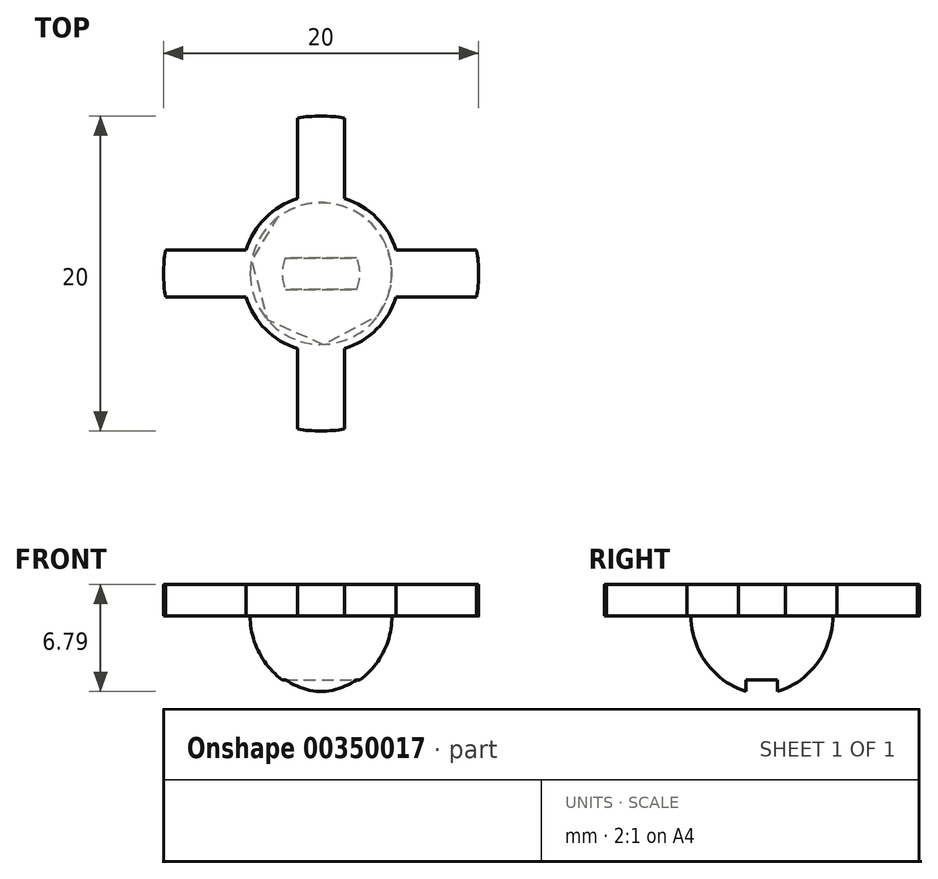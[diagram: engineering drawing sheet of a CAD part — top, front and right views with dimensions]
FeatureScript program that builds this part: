
annotation { "Feature Type Name" : "Feature", "Feature Type Description" : "" }
export const myFeature = defineFeature(function(context is Context, id is Id, definition is map)
    precondition{}
    {
        {
            var Q0;
            Q0=qCreatedBy(makeId("Top.planeOp"),FACE);
            var sketch = newSketch(context, id + "F0", { "sketchPlane" : qUnion([Q0])});
            skCircle(sketch, "E0", {"center": v(0, 0) * mm, "radius": 10 * mm});
            skSolve(sketch);
        }
        {
            var Q0;
            Q0=makeQuery(id+"F0.imprint","IMPRINT",FACE,{"disambiguationData":[TD([[makeQuery(id+"F0.imprint","IMPRINT",EDGE,{"derivedFrom":sQuery(id+"F0.wireOp",EDGE,"E0")}),1.0]])]});
            var Q1;
            Q1=sQuery(id+"F0.wireOp",EDGE,"E0");
            extrude(context, id + "F1", {"entities" : qUnion([Q0]), "surfaceEntities" : qUnion([Q1]), "depth" : 2 * mm});
        }
        {
            var Q0;
            Q0=makeQuery(id+"F1.opExtrude","CAP_FACE",FACE,{"disambiguationData":[OSD([sQuery(id+"F0.wireOp",EDGE,"E0")])],"isStart":false});
            var sketch = newSketch(context, id + "F2", { "sketchPlane" : qUnion([Q0])});
            skCircle(sketch, "E1", {"center": v(0, 0) * mm, "radius": 5 * mm});
            skLineSegment(sketch, "E2.bottom", {"start": v(-1.5, 10) * mm, "end": v(1.5, 10) * mm});
            skLineSegment(sketch, "E2.top", {"start": v(-1.5, -10) * mm, "end": v(1.5, -10) * mm});
            skLineSegment(sketch, "E2.left", {"start": v(-1.5, 10) * mm, "end": v(-1.5, -10) * mm});
            skLineSegment(sketch, "E2.right", {"start": v(1.5, 10) * mm, "end": v(1.5, -10) * mm});
            skLineSegment(sketch, "E3", {"start": v(0, 10) * mm, "end": v(0, -10) * mm, "construction": true});
            skLineSegment(sketch, "E4", {"start": v(-10, 0) * mm, "end": v(10, 0) * mm, "construction": true});
            skLineSegment(sketch, "E5.bottom", {"start": v(-10, 1.5) * mm, "end": v(10, 1.5) * mm});
            skLineSegment(sketch, "E5.top", {"start": v(-10, -1.5) * mm, "end": v(10, -1.5) * mm});
            skLineSegment(sketch, "E5.left", {"start": v(-10, 1.5) * mm, "end": v(-10, -1.5) * mm});
            skLineSegment(sketch, "E5.right", {"start": v(10, 1.5) * mm, "end": v(10, -1.5) * mm});
            skSolve(sketch);
        }
        {
            var Q0;
            {var subQ0=sQuery(id+"F2.wireOp",EDGE,"E2.left");var subQ1=sQuery(id+"F2.wireOp",EDGE,"E1");var subQ2=makeQuery(id+"F2.imprint","INTERSECT",VERTEX,{"disambiguationData":[OD(0.0)],"derivedFrom":[subQ1,subQ0]});Q0=makeQuery(id+"F2.imprint","IMPRINT",FACE,{"disambiguationData":[TD([[makeQuery(id+"F2.imprint","IMPRINT",EDGE,{"disambiguationData":[TD([[subQ2,-1.0]])],"derivedFrom":subQ1}),-1.0]])]});}
            var Q1;
            {var subQ0=sQuery(id+"F2.wireOp",EDGE,"E2.right");var subQ1=sQuery(id+"F2.wireOp",EDGE,"E1");var subQ2=makeQuery(id+"F2.imprint","INTERSECT",VERTEX,{"disambiguationData":[OD(0.0)],"derivedFrom":[subQ1,subQ0]});Q1=makeQuery(id+"F2.imprint","IMPRINT",FACE,{"disambiguationData":[TD([[makeQuery(id+"F2.imprint","IMPRINT",EDGE,{"disambiguationData":[TD([[subQ2,1.0]])],"derivedFrom":subQ1}),-1.0]])]});}
            var Q2;
            {var subQ0=sQuery(id+"F2.wireOp",EDGE,"E2.right");var subQ1=sQuery(id+"F2.wireOp",EDGE,"E1");var subQ2=makeQuery(id+"F2.imprint","INTERSECT",VERTEX,{"disambiguationData":[OD(1.0)],"derivedFrom":[subQ1,subQ0]});Q2=makeQuery(id+"F2.imprint","IMPRINT",FACE,{"disambiguationData":[TD([[makeQuery(id+"F2.imprint","IMPRINT",EDGE,{"disambiguationData":[TD([[subQ2,-1.0]])],"derivedFrom":subQ1}),-1.0]])]});}
            var Q3;
            {var subQ0=sQuery(id+"F2.wireOp",EDGE,"E5.top");var subQ1=sQuery(id+"F2.wireOp",EDGE,"E1");var subQ2=makeQuery(id+"F2.imprint","INTERSECT",VERTEX,{"disambiguationData":[OD(0.0)],"derivedFrom":[subQ1,subQ0]});Q3=makeQuery(id+"F2.imprint","IMPRINT",FACE,{"disambiguationData":[TD([[makeQuery(id+"F2.imprint","IMPRINT",EDGE,{"disambiguationData":[TD([[subQ2,-1.0]])],"derivedFrom":subQ1}),-1.0]])]});}
            extrude(context, id + "F3", {"entities" : qUnion([Q0, Q1, Q2, Q3]), "operationType" : NewBodyOperationType.REMOVE, "endBound" : BoundingType.THROUGH_ALL, "oppositeDirection" : true, "depth" : 25 * mm});
        }
        {
            var Q0;
            Q0=qCreatedBy(makeId("Right.planeOp"),FACE);
            var sketch = newSketch(context, id + "F4", { "sketchPlane" : qUnion([Q0])});
            skLineSegment(sketch, "E6", {"start": v(0, 0) * mm, "end": v(0, -5) * mm});
            skLineSegment(sketch, "E7", {"start": v(0, 0) * mm, "end": v(4.5, 0) * mm});
            skArc(sketch, "E8", {"start": v(0, -5) * mm, "mid": v(3.22, -3.37) * mm, "end": v(4.5, 0) * mm});
            skLineSegment(sketch, "E9", {"start": v(0, 0) * mm, "end": v(0, 4.05) * mm, "construction": true});
            skSolve(sketch);
        }
        {
            var Q0;
            Q0=makeQuery(id+"F4.imprint","IMPRINT",FACE,{"disambiguationData":[TD([[makeQuery(id+"F4.imprint","IMPRINT",EDGE,{"derivedFrom":sQuery(id+"F4.wireOp",EDGE,"E6")}),1.0]])]});
            var Q1;
            Q1=sQuery(id+"F4.wireOp",EDGE,"E9");
            revolve(context, id + "F5", {"operationType" : NewBodyOperationType.ADD, "entities" : qUnion([Q0]), "axis" : qUnion([Q1]), "revolveType" : RevolveType.FULL});
        }
        {
            var Q0;
            Q0=qCreatedBy(makeId("Front.planeOp"),FACE);
            var sketch = newSketch(context, id + "F6", { "sketchPlane" : qUnion([Q0])});
            skLineSegment(sketch, "E10.bottom", {"start": v(-3.18, -4.05) * mm, "end": v(3.18, -4.05) * mm});
            skLineSegment(sketch, "E10.top", {"start": v(-3.18, -6.05) * mm, "end": v(3.18, -6.05) * mm});
            skLineSegment(sketch, "E10.left", {"start": v(-3.18, -4.05) * mm, "end": v(-3.18, -6.05) * mm});
            skLineSegment(sketch, "E10.right", {"start": v(3.18, -4.05) * mm, "end": v(3.18, -6.05) * mm});
            skPoint(sketch, "E10.middle", {"position": v(0, -5.05) * mm});
            skSolve(sketch);
        }
        {
            var Q0;
            Q0=makeQuery(id+"F6.imprint","IMPRINT",FACE,{"disambiguationData":[TD([[makeQuery(id+"F6.imprint","IMPRINT",EDGE,{"derivedFrom":sQuery(id+"F6.wireOp",EDGE,"E10.bottom")}),-1.0]])]});
            extrude(context, id + "F7", {"entities" : qUnion([Q0]), "operationType" : NewBodyOperationType.REMOVE, "endBound" : BoundingType.SYMMETRIC, "depth" : 2 * mm});
        }
    });
